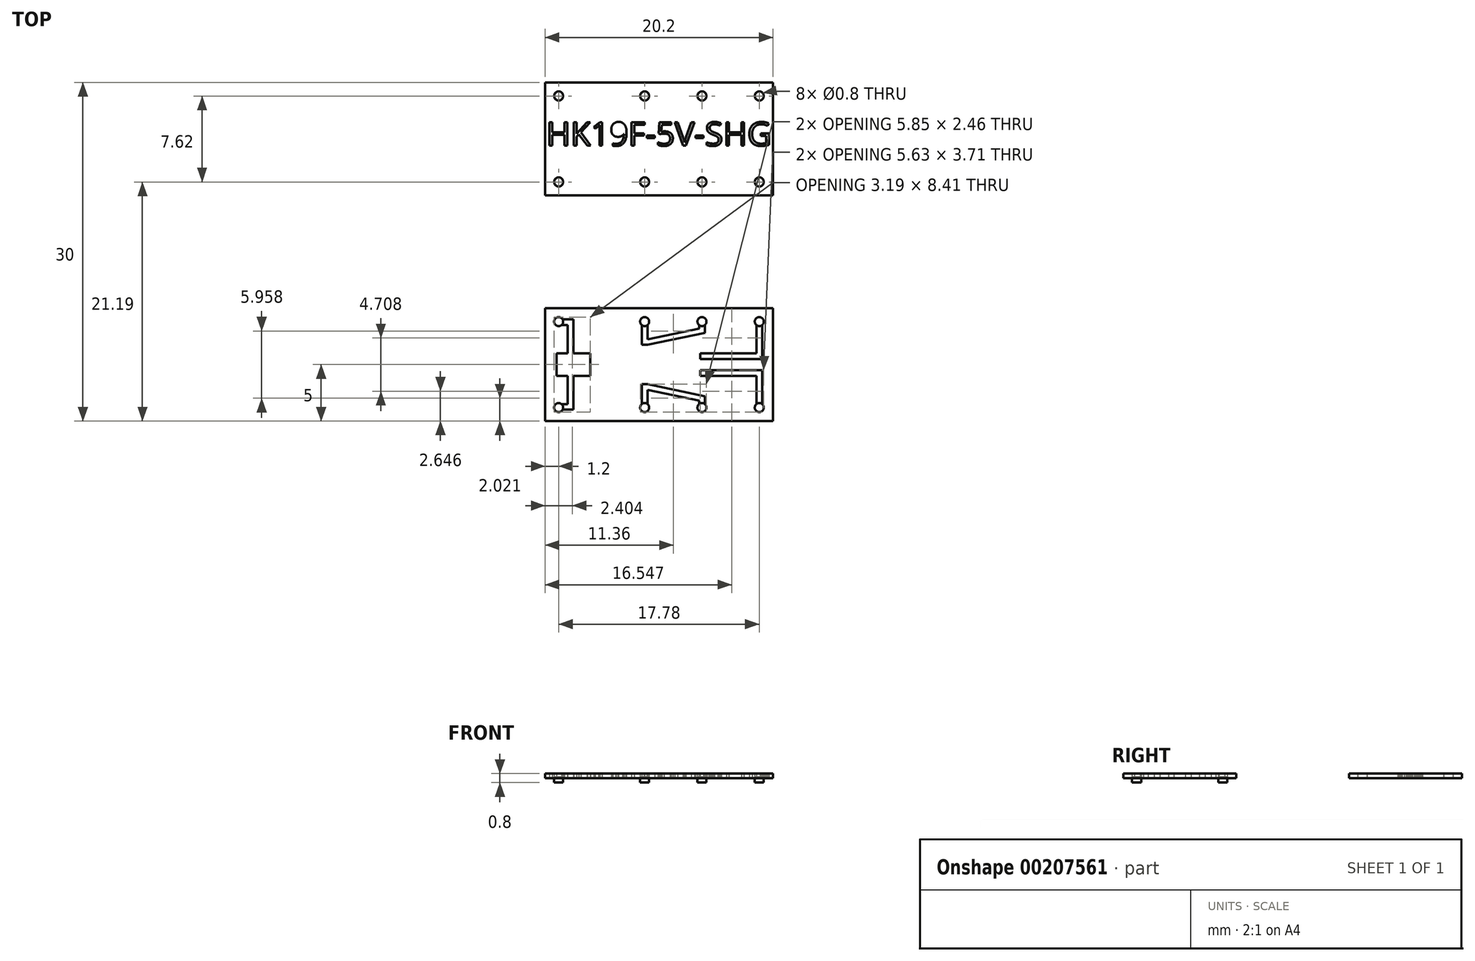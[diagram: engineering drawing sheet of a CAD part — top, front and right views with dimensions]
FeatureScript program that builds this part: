
annotation { "Feature Type Name" : "Feature", "Feature Type Description" : "" }
export const myFeature = defineFeature(function(context is Context, id is Id, definition is map)
    precondition{}
    {
        {
            var Q0;
            Q0=qCreatedBy(makeId("Top.planeOp"),FACE);
            var sketch = newSketch(context, id + "F0", { "sketchPlane" : qUnion([Q0])});
            skLineSegment(sketch, "E0.bottom", {"start": v(10.1, 5) * mm, "end": v(-10.1, 5) * mm});
            skLineSegment(sketch, "E0.top", {"start": v(10.1, -5) * mm, "end": v(-10.1, -5) * mm});
            skLineSegment(sketch, "E0.left", {"start": v(10.1, 5) * mm, "end": v(10.1, -5) * mm});
            skLineSegment(sketch, "E0.right", {"start": v(-10.1, 5) * mm, "end": v(-10.1, -5) * mm});
            skPoint(sketch, "E0.middle", {"position": v(0, 0) * mm});
            skCircle(sketch, "E1", {"center": v(-8.9, 3.81) * mm, "radius": 0.4 * mm});
            skCircle(sketch, "E2", {"center": v(-8.9, -3.8) * mm, "radius": 0.4 * mm});
            skCircle(sketch, "E3", {"center": v(-1.28, 3.81) * mm, "radius": 0.4 * mm});
            skCircle(sketch, "E4", {"center": v(-1.28, -3.8) * mm, "radius": 0.4 * mm});
            skCircle(sketch, "E5", {"center": v(3.8, -3.8) * mm, "radius": 0.4 * mm});
            skCircle(sketch, "E6", {"center": v(8.88, -3.8) * mm, "radius": 0.4 * mm});
            skCircle(sketch, "E7", {"center": v(3.8, 3.81) * mm, "radius": 0.4 * mm});
            skCircle(sketch, "E8", {"center": v(8.88, 3.81) * mm, "radius": 0.4 * mm});
            skText(sketch, "E9", { "text": "HK19F-5V-SHG", "fontName": "OpenSans-Regular.ttf"});
            skLineSegment(sketch, "E10.bottom", {"start": v(10.1, -15) * mm, "end": v(-10.1, -15) * mm});
            skLineSegment(sketch, "E10.top", {"start": v(10.1, -25) * mm, "end": v(-10.1, -25) * mm});
            skLineSegment(sketch, "E10.left", {"start": v(10.1, -15) * mm, "end": v(10.1, -25) * mm});
            skLineSegment(sketch, "E10.right", {"start": v(-10.1, -15) * mm, "end": v(-10.1, -25) * mm});
            skPoint(sketch, "E10.middle", {"position": v(0, -20) * mm});
            skCircle(sketch, "E11", {"center": v(-8.9, -16.19) * mm, "radius": 0.4 * mm});
            skCircle(sketch, "E12", {"center": v(-8.9, -23.8) * mm, "radius": 0.4 * mm});
            skCircle(sketch, "E13", {"center": v(-1.28, -16.19) * mm, "radius": 0.4 * mm});
            skCircle(sketch, "E14", {"center": v(-1.28, -23.8) * mm, "radius": 0.4 * mm});
            skCircle(sketch, "E15", {"center": v(3.8, -23.8) * mm, "radius": 0.4 * mm});
            skCircle(sketch, "E16", {"center": v(8.88, -23.8) * mm, "radius": 0.4 * mm});
            skCircle(sketch, "E17", {"center": v(3.8, -16.19) * mm, "radius": 0.4 * mm});
            skCircle(sketch, "E18", {"center": v(8.88, -16.19) * mm, "radius": 0.4 * mm});
            skLineSegment(sketch, "E19.bottom", {"start": v(-9.1, -19) * mm, "end": v(-6.1, -19) * mm});
            skLineSegment(sketch, "E19.top", {"start": v(-9.1, -21) * mm, "end": v(-6.1, -21) * mm});
            skLineSegment(sketch, "E19.left", {"start": v(-9.1, -19) * mm, "end": v(-9.1, -21) * mm});
            skLineSegment(sketch, "E19.right", {"start": v(-6.1, -19) * mm, "end": v(-6.1, -21) * mm});
            skPoint(sketch, "E19.middle", {"position": v(-7.6, -20) * mm});
            skLineSegment(sketch, "E20.bottom", {"start": v(-7.6, -19) * mm, "end": v(-8.1, -19) * mm});
            skLineSegment(sketch, "E20.top", {"start": v(-7.6, -16) * mm, "end": v(-8.1, -16) * mm});
            skLineSegment(sketch, "E20.left", {"start": v(-7.6, -19) * mm, "end": v(-7.6, -16) * mm});
            skLineSegment(sketch, "E20.right", {"start": v(-8.1, -19) * mm, "end": v(-8.1, -16) * mm});
            skLineSegment(sketch, "E21.bottom", {"start": v(-8.1, -16) * mm, "end": v(-8.65, -16) * mm});
            skLineSegment(sketch, "E21.top", {"start": v(-8.1, -16.5) * mm, "end": v(-8.65, -16.5) * mm});
            skLineSegment(sketch, "E21.left", {"start": v(-8.1, -16) * mm, "end": v(-8.1, -16.5) * mm});
            skLineSegment(sketch, "E21.right", {"start": v(-8.65, -16) * mm, "end": v(-8.65, -16.5) * mm});
            skLineSegment(sketch, "E22.bottom", {"start": v(-7.6, -21) * mm, "end": v(-8.1, -21) * mm});
            skLineSegment(sketch, "E22.top", {"start": v(-7.6, -24) * mm, "end": v(-8.1, -24) * mm});
            skLineSegment(sketch, "E22.left", {"start": v(-7.6, -21) * mm, "end": v(-7.6, -24) * mm});
            skLineSegment(sketch, "E22.right", {"start": v(-8.1, -21) * mm, "end": v(-8.1, -24) * mm});
            skLineSegment(sketch, "E23.bottom", {"start": v(-8.1, -24) * mm, "end": v(-8.65, -24) * mm});
            skLineSegment(sketch, "E23.top", {"start": v(-8.1, -23.5) * mm, "end": v(-8.65, -23.5) * mm});
            skLineSegment(sketch, "E23.left", {"start": v(-8.1, -24) * mm, "end": v(-8.1, -23.5) * mm});
            skLineSegment(sketch, "E23.right", {"start": v(-8.65, -24) * mm, "end": v(-8.65, -23.5) * mm});
            skLineSegment(sketch, "E24.bottom", {"start": v(9.13, -16.5) * mm, "end": v(8.63, -16.5) * mm});
            skLineSegment(sketch, "E24.top", {"start": v(9.13, -19) * mm, "end": v(8.63, -19) * mm});
            skLineSegment(sketch, "E24.left", {"start": v(9.13, -16.5) * mm, "end": v(9.13, -19) * mm});
            skLineSegment(sketch, "E24.right", {"start": v(8.63, -16.5) * mm, "end": v(8.63, -19) * mm});
            skLineSegment(sketch, "E25.bottom", {"start": v(9.13, -23.5) * mm, "end": v(8.63, -23.5) * mm});
            skLineSegment(sketch, "E25.top", {"start": v(9.13, -21) * mm, "end": v(8.63, -21) * mm});
            skLineSegment(sketch, "E25.left", {"start": v(9.13, -23.5) * mm, "end": v(9.13, -21) * mm});
            skLineSegment(sketch, "E25.right", {"start": v(8.63, -23.5) * mm, "end": v(8.63, -21) * mm});
            skLineSegment(sketch, "E26.bottom", {"start": v(9.13, -19) * mm, "end": v(3.63, -19) * mm});
            skLineSegment(sketch, "E26.top", {"start": v(9.13, -19.5) * mm, "end": v(3.63, -19.5) * mm});
            skLineSegment(sketch, "E26.left", {"start": v(9.13, -19) * mm, "end": v(9.13, -19.5) * mm});
            skLineSegment(sketch, "E26.right", {"start": v(3.63, -19) * mm, "end": v(3.63, -19.5) * mm});
            skLineSegment(sketch, "E27.bottom", {"start": v(9.13, -21) * mm, "end": v(3.63, -21) * mm});
            skLineSegment(sketch, "E27.top", {"start": v(9.13, -20.5) * mm, "end": v(3.63, -20.5) * mm});
            skLineSegment(sketch, "E27.left", {"start": v(9.13, -21) * mm, "end": v(9.13, -20.5) * mm});
            skLineSegment(sketch, "E27.right", {"start": v(3.63, -21) * mm, "end": v(3.63, -20.5) * mm});
            skLineSegment(sketch, "E28.bottom", {"start": v(3.55, -23.5) * mm, "end": v(4.05, -23.5) * mm});
            skLineSegment(sketch, "E28.top", {"start": v(3.55, -23.2) * mm, "end": v(4.05, -23.2) * mm});
            skLineSegment(sketch, "E28.left", {"start": v(3.55, -23.5) * mm, "end": v(3.55, -23.2) * mm});
            skLineSegment(sketch, "E28.right", {"start": v(4.05, -23.5) * mm, "end": v(4.05, -23.2) * mm});
            skLineSegment(sketch, "E29.bottom", {"start": v(3.55, -16.5) * mm, "end": v(4.05, -16.5) * mm});
            skLineSegment(sketch, "E29.top", {"start": v(3.55, -16.8) * mm, "end": v(4.05, -16.8) * mm});
            skLineSegment(sketch, "E29.left", {"start": v(3.55, -16.5) * mm, "end": v(3.55, -16.8) * mm});
            skLineSegment(sketch, "E29.right", {"start": v(4.05, -16.5) * mm, "end": v(4.05, -16.8) * mm});
            skLineSegment(sketch, "E30.bottom", {"start": v(-1.53, -16.5) * mm, "end": v(-1.03, -16.5) * mm});
            skLineSegment(sketch, "E30.top", {"start": v(-1.53, -18.25) * mm, "end": v(-1.03, -18.25) * mm});
            skLineSegment(sketch, "E30.left", {"start": v(-1.53, -16.5) * mm, "end": v(-1.53, -18.25) * mm});
            skLineSegment(sketch, "E30.right", {"start": v(-1.03, -16.5) * mm, "end": v(-1.03, -18.25) * mm});
            skLineSegment(sketch, "E31.bottom", {"start": v(-1.53, -23.5) * mm, "end": v(-1.03, -23.5) * mm});
            skLineSegment(sketch, "E31.top", {"start": v(-1.53, -21.75) * mm, "end": v(-1.03, -21.75) * mm});
            skLineSegment(sketch, "E31.left", {"start": v(-1.53, -23.5) * mm, "end": v(-1.53, -21.75) * mm});
            skLineSegment(sketch, "E31.right", {"start": v(-1.03, -23.5) * mm, "end": v(-1.03, -21.75) * mm});
            skLineSegment(sketch, "E32", {"start": v(-1.03, -18.25) * mm, "end": v(4.05, -17.2) * mm});
            skLineSegment(sketch, "E33", {"start": v(-1.03, -17.75) * mm, "end": v(3.55, -16.8) * mm});
            skLineSegment(sketch, "E34", {"start": v(-1.03, -21.75) * mm, "end": v(4.05, -22.8) * mm});
            skLineSegment(sketch, "E35", {"start": v(-1.03, -22.25) * mm, "end": v(3.55, -23.2) * mm});
            skLineSegment(sketch, "E36", {"start": v(4.05, -22.8) * mm, "end": v(4.05, -23.2) * mm});
            skLineSegment(sketch, "E37", {"start": v(4.05, -17.2) * mm, "end": v(4.05, -16.8) * mm});
            const initialGuessF0  = {"E9": [-0.01, -0.0006, 1, 0, 0.0021]};
            skSetInitialGuess(sketch, initialGuessF0);
            skSolve(sketch);
        }
        {
            var Q0;
            Q0=makeQuery(id+"F0.imprint","IMPRINT",FACE,{"disambiguationData":[TD([[makeQuery(id+"F0.imprint","IMPRINT",EDGE,{"derivedFrom":sQuery(id+"F0.wireOp",EDGE,"E0.bottom")}),1.0]])]});
            extrude(context, id + "F1", {"entities" : qUnion([Q0]), "depth" : .4 * mm});
        }
        {
            var Q0;
            Q0=makeQuery(id+"F0.imprint","IMPRINT",FACE,{"disambiguationData":[TD([[makeQuery(id+"F0.imprint","IMPRINT",EDGE,{"derivedFrom":sQuery(id+"F0.wireOp",EDGE,"E10.bottom")}),1.0]])]});
            extrude(context, id + "F2", {"entities" : qUnion([Q0]), "depth" : .4 * mm});
        }
        {
            var Q0;
            {var subQ0=sQuery(id+"F0.wireOp",EDGE,"E24.bottom");Q0=makeQuery(id+"F0.imprint","IMPRINT",FACE,{"disambiguationData":[TD([[makeQuery(id+"F0.imprint","IMPRINT",EDGE,{"derivedFrom":subQ0}),-1.0]])]});}
            var Q1;
            {var subQ0=sQuery(id+"F0.wireOp",EDGE,"E24.bottom");Q1=makeQuery(id+"F0.imprint","IMPRINT",FACE,{"disambiguationData":[TD([[makeQuery(id+"F0.imprint","IMPRINT",EDGE,{"derivedFrom":subQ0}),1.0]])]});}
            var Q2;
            {var subQ0=sQuery(id+"F0.wireOp",EDGE,"E29.bottom");Q2=makeQuery(id+"F0.imprint","IMPRINT",FACE,{"disambiguationData":[TD([[makeQuery(id+"F0.imprint","IMPRINT",EDGE,{"derivedFrom":subQ0}),1.0]])]});}
            var Q3;
            {var subQ0=sQuery(id+"F0.wireOp",EDGE,"E29.bottom");Q3=makeQuery(id+"F0.imprint","IMPRINT",FACE,{"disambiguationData":[TD([[makeQuery(id+"F0.imprint","IMPRINT",EDGE,{"derivedFrom":subQ0}),-1.0]])]});}
            var Q4;
            {var subQ0=sQuery(id+"F0.wireOp",EDGE,"E30.bottom");Q4=makeQuery(id+"F0.imprint","IMPRINT",FACE,{"disambiguationData":[TD([[makeQuery(id+"F0.imprint","IMPRINT",EDGE,{"derivedFrom":subQ0}),1.0]])]});}
            var Q5;
            {var subQ0=sQuery(id+"F0.wireOp",EDGE,"E30.bottom");Q5=makeQuery(id+"F0.imprint","IMPRINT",FACE,{"disambiguationData":[TD([[makeQuery(id+"F0.imprint","IMPRINT",EDGE,{"derivedFrom":subQ0}),-1.0]])]});}
            var Q6;
            {var subQ0=sQuery(id+"F0.wireOp",EDGE,"E21.right");Q6=makeQuery(id+"F0.imprint","IMPRINT",FACE,{"disambiguationData":[TD([[makeQuery(id+"F0.imprint","IMPRINT",EDGE,{"derivedFrom":subQ0}),-1.0]])]});}
            var Q7;
            {var subQ0=sQuery(id+"F0.wireOp",EDGE,"E21.right");Q7=makeQuery(id+"F0.imprint","IMPRINT",FACE,{"disambiguationData":[TD([[makeQuery(id+"F0.imprint","IMPRINT",EDGE,{"derivedFrom":subQ0}),1.0]])]});}
            var Q8;
            {var subQ0=sQuery(id+"F0.wireOp",EDGE,"E23.right");Q8=makeQuery(id+"F0.imprint","IMPRINT",FACE,{"disambiguationData":[TD([[makeQuery(id+"F0.imprint","IMPRINT",EDGE,{"derivedFrom":subQ0}),1.0]])]});}
            var Q9;
            {var subQ0=sQuery(id+"F0.wireOp",EDGE,"E23.right");Q9=makeQuery(id+"F0.imprint","IMPRINT",FACE,{"disambiguationData":[TD([[makeQuery(id+"F0.imprint","IMPRINT",EDGE,{"derivedFrom":subQ0}),-1.0]])]});}
            var Q10;
            {var subQ0=sQuery(id+"F0.wireOp",EDGE,"E31.bottom");Q10=makeQuery(id+"F0.imprint","IMPRINT",FACE,{"disambiguationData":[TD([[makeQuery(id+"F0.imprint","IMPRINT",EDGE,{"derivedFrom":subQ0}),-1.0]])]});}
            var Q11;
            {var subQ0=sQuery(id+"F0.wireOp",EDGE,"E31.bottom");Q11=makeQuery(id+"F0.imprint","IMPRINT",FACE,{"disambiguationData":[TD([[makeQuery(id+"F0.imprint","IMPRINT",EDGE,{"derivedFrom":subQ0}),1.0]])]});}
            var Q12;
            {var subQ0=sQuery(id+"F0.wireOp",EDGE,"E28.bottom");Q12=makeQuery(id+"F0.imprint","IMPRINT",FACE,{"disambiguationData":[TD([[makeQuery(id+"F0.imprint","IMPRINT",EDGE,{"derivedFrom":subQ0}),1.0]])]});}
            var Q13;
            {var subQ0=sQuery(id+"F0.wireOp",EDGE,"E28.bottom");Q13=makeQuery(id+"F0.imprint","IMPRINT",FACE,{"disambiguationData":[TD([[makeQuery(id+"F0.imprint","IMPRINT",EDGE,{"derivedFrom":subQ0}),-1.0]])]});}
            var Q14;
            {var subQ0=sQuery(id+"F0.wireOp",EDGE,"E25.bottom");Q14=makeQuery(id+"F0.imprint","IMPRINT",FACE,{"disambiguationData":[TD([[makeQuery(id+"F0.imprint","IMPRINT",EDGE,{"derivedFrom":subQ0}),-1.0]])]});}
            var Q15;
            {var subQ0=sQuery(id+"F0.wireOp",EDGE,"E25.bottom");Q15=makeQuery(id+"F0.imprint","IMPRINT",FACE,{"disambiguationData":[TD([[makeQuery(id+"F0.imprint","IMPRINT",EDGE,{"derivedFrom":subQ0}),1.0]])]});}
            extrude(context, id + "F3", {"entities" : qUnion([Q0, Q1, Q2, Q3, Q4, Q5, Q6, Q7, Q8, Q9, Q10, Q11, Q12, Q13, Q14, Q15]), "operationType" : NewBodyOperationType.ADD, "depth" : .1 * mm});
        }
        {
            var Q0;
            {var subQ0=sQuery(id+"F0.wireOp",EDGE,"E23.right");Q0=makeQuery(id+"F0.imprint","IMPRINT",FACE,{"disambiguationData":[TD([[makeQuery(id+"F0.imprint","IMPRINT",EDGE,{"derivedFrom":subQ0}),1.0]])]});}
            var Q1;
            {var subQ0=sQuery(id+"F0.wireOp",EDGE,"E23.right");Q1=makeQuery(id+"F0.imprint","IMPRINT",FACE,{"disambiguationData":[TD([[makeQuery(id+"F0.imprint","IMPRINT",EDGE,{"derivedFrom":subQ0}),-1.0]])]});}
            var Q2;
            {var subQ0=sQuery(id+"F0.wireOp",EDGE,"E31.bottom");Q2=makeQuery(id+"F0.imprint","IMPRINT",FACE,{"disambiguationData":[TD([[makeQuery(id+"F0.imprint","IMPRINT",EDGE,{"derivedFrom":subQ0}),-1.0]])]});}
            var Q3;
            {var subQ0=sQuery(id+"F0.wireOp",EDGE,"E31.bottom");Q3=makeQuery(id+"F0.imprint","IMPRINT",FACE,{"disambiguationData":[TD([[makeQuery(id+"F0.imprint","IMPRINT",EDGE,{"derivedFrom":subQ0}),1.0]])]});}
            var Q4;
            {var subQ0=sQuery(id+"F0.wireOp",EDGE,"E28.bottom");Q4=makeQuery(id+"F0.imprint","IMPRINT",FACE,{"disambiguationData":[TD([[makeQuery(id+"F0.imprint","IMPRINT",EDGE,{"derivedFrom":subQ0}),-1.0]])]});}
            var Q5;
            {var subQ0=sQuery(id+"F0.wireOp",EDGE,"E28.bottom");Q5=makeQuery(id+"F0.imprint","IMPRINT",FACE,{"disambiguationData":[TD([[makeQuery(id+"F0.imprint","IMPRINT",EDGE,{"derivedFrom":subQ0}),1.0]])]});}
            var Q6;
            {var subQ0=sQuery(id+"F0.wireOp",EDGE,"E25.bottom");Q6=makeQuery(id+"F0.imprint","IMPRINT",FACE,{"disambiguationData":[TD([[makeQuery(id+"F0.imprint","IMPRINT",EDGE,{"derivedFrom":subQ0}),1.0]])]});}
            var Q7;
            {var subQ0=sQuery(id+"F0.wireOp",EDGE,"E25.bottom");Q7=makeQuery(id+"F0.imprint","IMPRINT",FACE,{"disambiguationData":[TD([[makeQuery(id+"F0.imprint","IMPRINT",EDGE,{"derivedFrom":subQ0}),-1.0]])]});}
            var Q8;
            {var subQ0=sQuery(id+"F0.wireOp",EDGE,"E24.bottom");Q8=makeQuery(id+"F0.imprint","IMPRINT",FACE,{"disambiguationData":[TD([[makeQuery(id+"F0.imprint","IMPRINT",EDGE,{"derivedFrom":subQ0}),1.0]])]});}
            var Q9;
            {var subQ0=sQuery(id+"F0.wireOp",EDGE,"E24.bottom");Q9=makeQuery(id+"F0.imprint","IMPRINT",FACE,{"disambiguationData":[TD([[makeQuery(id+"F0.imprint","IMPRINT",EDGE,{"derivedFrom":subQ0}),-1.0]])]});}
            var Q10;
            {var subQ0=sQuery(id+"F0.wireOp",EDGE,"E29.bottom");Q10=makeQuery(id+"F0.imprint","IMPRINT",FACE,{"disambiguationData":[TD([[makeQuery(id+"F0.imprint","IMPRINT",EDGE,{"derivedFrom":subQ0}),-1.0]])]});}
            var Q11;
            {var subQ0=sQuery(id+"F0.wireOp",EDGE,"E29.bottom");Q11=makeQuery(id+"F0.imprint","IMPRINT",FACE,{"disambiguationData":[TD([[makeQuery(id+"F0.imprint","IMPRINT",EDGE,{"derivedFrom":subQ0}),1.0]])]});}
            var Q12;
            {var subQ0=sQuery(id+"F0.wireOp",EDGE,"E30.bottom");Q12=makeQuery(id+"F0.imprint","IMPRINT",FACE,{"disambiguationData":[TD([[makeQuery(id+"F0.imprint","IMPRINT",EDGE,{"derivedFrom":subQ0}),-1.0]])]});}
            var Q13;
            {var subQ0=sQuery(id+"F0.wireOp",EDGE,"E30.bottom");Q13=makeQuery(id+"F0.imprint","IMPRINT",FACE,{"disambiguationData":[TD([[makeQuery(id+"F0.imprint","IMPRINT",EDGE,{"derivedFrom":subQ0}),1.0]])]});}
            var Q14;
            {var subQ0=sQuery(id+"F0.wireOp",EDGE,"E21.right");Q14=makeQuery(id+"F0.imprint","IMPRINT",FACE,{"disambiguationData":[TD([[makeQuery(id+"F0.imprint","IMPRINT",EDGE,{"derivedFrom":subQ0}),1.0]])]});}
            var Q15;
            {var subQ0=sQuery(id+"F0.wireOp",EDGE,"E21.right");Q15=makeQuery(id+"F0.imprint","IMPRINT",FACE,{"disambiguationData":[TD([[makeQuery(id+"F0.imprint","IMPRINT",EDGE,{"derivedFrom":subQ0}),-1.0]])]});}
            extrude(context, id + "F4", {"entities" : qUnion([Q0, Q1, Q2, Q3, Q4, Q5, Q6, Q7, Q8, Q9, Q10, Q11, Q12, Q13, Q14, Q15]), "operationType" : NewBodyOperationType.ADD, "oppositeDirection" : true, "depth" : .4 * mm});
        }
    });
